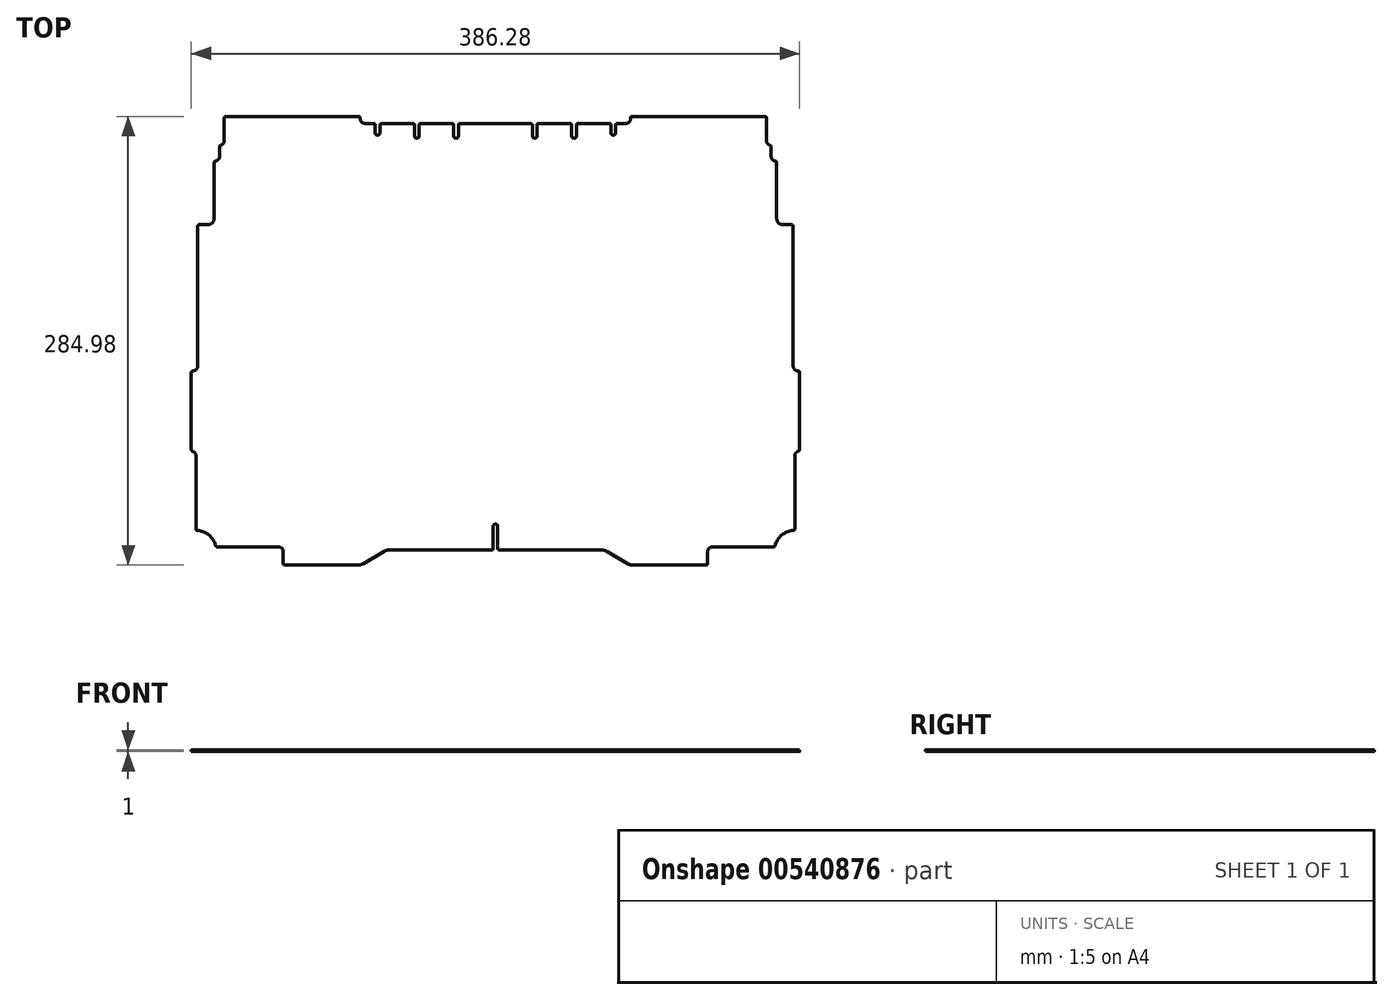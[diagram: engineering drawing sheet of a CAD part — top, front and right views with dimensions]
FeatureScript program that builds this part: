
annotation { "Feature Type Name" : "Feature", "Feature Type Description" : "" }
export const myFeature = defineFeature(function(context is Context, id is Id, definition is map)
    precondition{}
    {
        {
            var Q0;
            Q0=qCreatedBy(makeId("Top.planeOp"),FACE);
            var sketch = newSketch(context, id + "F0", { "sketchPlane" : qUnion([Q0])});
            skLineSegment(sketch, "E0", {"start": v(-80.67, -133.5) * mm, "end": v(-41, -133.5) * mm});
            skLineSegment(sketch, "E1", {"start": v(-38, -136.5) * mm, "end": v(-38, -144.99) * mm});
            skLineSegment(sketch, "E2", {"start": v(-38, -144.99) * mm, "end": v(11.4, -144.99) * mm});
            skLineSegment(sketch, "E3", {"start": v(11.4, -144.99) * mm, "end": v(25.96, -136.34) * mm});
            skLineSegment(sketch, "E4", {"start": v(29.02, -135.5) * mm, "end": v(95.25, -135.5) * mm});
            skLineSegment(sketch, "E5", {"start": v(-93.4, -123.03) * mm, "end": v(-93.4, -75.62) * mm});
            skLineSegment(sketch, "E6", {"start": v(-96.4, -72.62) * mm, "end": v(-96.4, -21.71) * mm});
            skLineSegment(sketch, "E7", {"start": v(-96.4, -21.71) * mm, "end": v(-95.4, -21.71) * mm});
            skLineSegment(sketch, "E8", {"start": v(-92.4, -18.72) * mm, "end": v(-92.4, 71.11) * mm});
            skLineSegment(sketch, "E9", {"start": v(-92.4, 71.11) * mm, "end": v(-85.91, 71.11) * mm});
            skLineSegment(sketch, "E10", {"start": v(-81.92, 75.1) * mm, "end": v(-81.92, 111.54) * mm});
            skLineSegment(sketch, "E11", {"start": v(-81.92, 111.54) * mm, "end": v(-81.42, 111.54) * mm});
            skLineSegment(sketch, "E12", {"start": v(-78.43, 114.53) * mm, "end": v(-78.43, 121.52) * mm});
            skLineSegment(sketch, "E13", {"start": v(-75.43, 124.52) * mm, "end": v(-75.43, 139.99) * mm});
            skLineSegment(sketch, "E14", {"start": v(-75.43, 139.99) * mm, "end": v(10.9, 139.99) * mm});
            skLineSegment(sketch, "E15", {"start": v(10.9, 139.99) * mm, "end": v(10.9, 138.49) * mm});
            skLineSegment(sketch, "E16", {"start": v(13.9, 135.5) * mm, "end": v(20.4, 135.5) * mm});
            skLineSegment(sketch, "E17", {"start": v(96.75, 135.5) * mm, "end": v(96.75, -119.03) * mm});
            skArc(sketch, "E18", {"start": v(96.75, -119.03) * mm, "mid": v(95.7, -119.47) * mm, "end": v(95.25, -120.53) * mm});
            skLineSegment(sketch, "E19", {"start": v(95.25, -120.53) * mm, "end": v(95.25, -135.5) * mm});
            skArc(sketch, "E20", {"start": v(70.3, 127.51) * mm, "mid": v(71.8, 126.01) * mm, "end": v(73.3, 127.51) * mm});
            skLineSegment(sketch, "E21", {"start": v(73.3, 127.51) * mm, "end": v(73.3, 135.5) * mm});
            skLineSegment(sketch, "E22", {"start": v(70.3, 127.51) * mm, "end": v(70.3, 135.5) * mm});
            skLineSegment(sketch, "E23", {"start": v(73.3, 135.5) * mm, "end": v(96.75, 135.5) * mm});
            skLineSegment(sketch, "E24", {"start": v(48.34, 127.51) * mm, "end": v(48.34, 135.5) * mm});
            skLineSegment(sketch, "E25", {"start": v(45.34, 127.51) * mm, "end": v(45.34, 135.5) * mm});
            skArc(sketch, "E26", {"start": v(45.34, 127.51) * mm, "mid": v(46.84, 126.01) * mm, "end": v(48.34, 127.51) * mm});
            skLineSegment(sketch, "E27", {"start": v(23.39, 129.5) * mm, "end": v(23.39, 135.5) * mm});
            skLineSegment(sketch, "E28", {"start": v(20.4, 129.5) * mm, "end": v(20.4, 135.5) * mm});
            skLineSegment(sketch, "E29", {"start": v(48.34, 135.5) * mm, "end": v(70.3, 135.5) * mm});
            skLineSegment(sketch, "E30", {"start": v(23.39, 135.5) * mm, "end": v(45.34, 135.5) * mm});
            skArc(sketch, "E31", {"start": v(-85.91, 71.11) * mm, "mid": v(-83.09, 72.28) * mm, "end": v(-81.92, 75.1) * mm});
            skArc(sketch, "E32", {"start": v(10.9, 138.49) * mm, "mid": v(11.79, 136.37) * mm, "end": v(13.9, 135.5) * mm});
            skArc(sketch, "E33", {"start": v(-95.4, -21.71) * mm, "mid": v(-93.28, -20.84) * mm, "end": v(-92.4, -18.72) * mm});
            skArc(sketch, "E34", {"start": v(-93.4, -75.62) * mm, "mid": v(-94.28, -73.5) * mm, "end": v(-96.4, -72.62) * mm});
            skArc(sketch, "E35", {"start": v(-38, -136.5) * mm, "mid": v(-38.88, -134.39) * mm, "end": v(-41, -133.5) * mm});
            skArc(sketch, "E36", {"start": v(-81.42, 111.54) * mm, "mid": v(-79.3, 112.42) * mm, "end": v(-78.43, 114.53) * mm});
            skArc(sketch, "E37", {"start": v(-78.43, 121.52) * mm, "mid": v(-76.3, 122.4) * mm, "end": v(-75.43, 124.52) * mm});
            skArc(sketch, "E38", {"start": v(29.02, -135.5) * mm, "mid": v(27.44, -135.72) * mm, "end": v(25.96, -136.34) * mm});
            skArc(sketch, "E39", {"start": v(-80.67, -133.5) * mm, "mid": v(-85.15, -125.98) * mm, "end": v(-93.4, -123.03) * mm});
            skArc(sketch, "E40", {"start": v(20.4, 129.5) * mm, "mid": v(21.89, 128) * mm, "end": v(23.39, 129.5) * mm});
            skArc(sketch, "E41.MirrorCS", {"start": v(96.75, -119.03) * mm, "mid": v(97.8, -119.47) * mm, "end": v(98.25, -120.53) * mm});
            skLineSegment(sketch, "E42.MirrorCS", {"start": v(289.9, -21.71) * mm, "end": v(288.9, -21.71) * mm});
            skArc(sketch, "E43.MirrorCS", {"start": v(274.92, 111.54) * mm, "mid": v(272.8, 112.42) * mm, "end": v(271.93, 114.53) * mm});
            skLineSegment(sketch, "E44.MirrorCS", {"start": v(275.42, 111.54) * mm, "end": v(274.92, 111.54) * mm});
            skArc(sketch, "E45.MirrorCS", {"start": v(288.9, -21.71) * mm, "mid": v(286.78, -20.84) * mm, "end": v(285.9, -18.72) * mm});
            skArc(sketch, "E46.MirrorCS", {"start": v(123.2, 127.51) * mm, "mid": v(121.7, 126.01) * mm, "end": v(120.2, 127.51) * mm});
            skArc(sketch, "E47.MirrorCS", {"start": v(148.16, 127.51) * mm, "mid": v(146.66, 126.01) * mm, "end": v(145.16, 127.51) * mm});
            skLineSegment(sketch, "E48.MirrorCS", {"start": v(231.5, -136.5) * mm, "end": v(231.5, -144.99) * mm});
            skLineSegment(sketch, "E49.MirrorCS", {"start": v(173.1, 129.5) * mm, "end": v(173.1, 135.5) * mm});
            skLineSegment(sketch, "E50.MirrorCS", {"start": v(148.16, 127.51) * mm, "end": v(148.16, 135.5) * mm});
            skLineSegment(sketch, "E51.MirrorCS", {"start": v(123.2, 127.51) * mm, "end": v(123.2, 135.5) * mm});
            skLineSegment(sketch, "E52.MirrorCS", {"start": v(271.93, 114.53) * mm, "end": v(271.93, 121.52) * mm});
            skArc(sketch, "E53.MirrorCS", {"start": v(164.48, -135.5) * mm, "mid": v(166.06, -135.72) * mm, "end": v(167.54, -136.34) * mm});
            skLineSegment(sketch, "E54.MirrorCS", {"start": v(179.6, 135.5) * mm, "end": v(173.1, 135.5) * mm});
            skArc(sketch, "E55.MirrorCS", {"start": v(279.41, 71.11) * mm, "mid": v(276.59, 72.28) * mm, "end": v(275.42, 75.1) * mm});
            skLineSegment(sketch, "E56.MirrorCS", {"start": v(145.16, 127.51) * mm, "end": v(145.16, 135.5) * mm});
            skArc(sketch, "E57.MirrorCS", {"start": v(231.5, -136.5) * mm, "mid": v(232.38, -134.39) * mm, "end": v(234.5, -133.5) * mm});
            skLineSegment(sketch, "E58.MirrorCS", {"start": v(285.9, 71.11) * mm, "end": v(279.41, 71.11) * mm});
            skArc(sketch, "E59.MirrorCS", {"start": v(182.6, 138.49) * mm, "mid": v(181.71, 136.37) * mm, "end": v(179.6, 135.5) * mm});
            skLineSegment(sketch, "E60.MirrorCS", {"start": v(182.6, 139.99) * mm, "end": v(182.6, 138.49) * mm});
            skArc(sketch, "E61.MirrorCS", {"start": v(271.93, 121.52) * mm, "mid": v(269.8, 122.4) * mm, "end": v(268.93, 124.52) * mm});
            skArc(sketch, "E62.MirrorCS", {"start": v(173.1, 129.5) * mm, "mid": v(171.61, 128) * mm, "end": v(170.11, 129.5) * mm});
            skArc(sketch, "E63.MirrorCS", {"start": v(286.9, -75.62) * mm, "mid": v(287.78, -73.5) * mm, "end": v(289.9, -72.62) * mm});
            skLineSegment(sketch, "E64.MirrorCS", {"start": v(120.2, 127.51) * mm, "end": v(120.2, 135.5) * mm});
            skLineSegment(sketch, "E65.MirrorCS", {"start": v(170.11, 129.5) * mm, "end": v(170.11, 135.5) * mm});
            skLineSegment(sketch, "E66.MirrorCS", {"start": v(268.93, 124.52) * mm, "end": v(268.93, 139.99) * mm});
            skLineSegment(sketch, "E67.MirrorCS", {"start": v(98.25, -120.53) * mm, "end": v(98.25, -135.5) * mm});
            skLineSegment(sketch, "E68.MirrorCS", {"start": v(231.5, -144.99) * mm, "end": v(182.1, -144.99) * mm});
            skLineSegment(sketch, "E69.MirrorCS", {"start": v(145.16, 135.5) * mm, "end": v(123.2, 135.5) * mm});
            skLineSegment(sketch, "E70.MirrorCS", {"start": v(268.93, 139.99) * mm, "end": v(182.6, 139.99) * mm});
            skLineSegment(sketch, "E71.MirrorCS", {"start": v(164.48, -135.5) * mm, "end": v(98.25, -135.5) * mm});
            skLineSegment(sketch, "E72.MirrorCS", {"start": v(286.9, -123.03) * mm, "end": v(286.9, -75.62) * mm});
            skLineSegment(sketch, "E73.MirrorCS", {"start": v(170.11, 135.5) * mm, "end": v(148.16, 135.5) * mm});
            skLineSegment(sketch, "E74.MirrorCS", {"start": v(274.17, -133.5) * mm, "end": v(234.5, -133.5) * mm});
            skArc(sketch, "E75.MirrorCS", {"start": v(274.17, -133.5) * mm, "mid": v(278.65, -125.98) * mm, "end": v(286.9, -123.03) * mm});
            skLineSegment(sketch, "E76.MirrorCS", {"start": v(275.42, 75.1) * mm, "end": v(275.42, 111.54) * mm});
            skLineSegment(sketch, "E77.MirrorCS", {"start": v(182.1, -144.99) * mm, "end": v(167.54, -136.34) * mm});
            skLineSegment(sketch, "E78.MirrorCS", {"start": v(289.9, -72.62) * mm, "end": v(289.9, -21.71) * mm});
            skLineSegment(sketch, "E79.MirrorCS", {"start": v(285.9, -18.72) * mm, "end": v(285.9, 71.11) * mm});
            skLineSegment(sketch, "E80.MirrorCS", {"start": v(120.2, 135.5) * mm, "end": v(96.75, 135.5) * mm});
            skSolve(sketch);
        }
        {
            var Q0;
            Q0=makeQuery(id+"F0.imprint","IMPRINT",FACE,{"disambiguationData":[TD([[makeQuery(id+"F0.imprint","IMPRINT",EDGE,{"derivedFrom":sQuery(id+"F0.wireOp",EDGE,"E0")}),1.0]])]});
            var Q1;
            Q1=makeQuery(id+"F0.imprint","IMPRINT",FACE,{"disambiguationData":[TD([[makeQuery(id+"F0.imprint","IMPRINT",EDGE,{"derivedFrom":sQuery(id+"F0.wireOp",EDGE,"E17")}),1.0]])]});
            extrude(context, id + "F1", {"entities" : qUnion([Q0, Q1]), "depth" : 1 * mm, "offsetDistance" : 25 * mm});
        }
        {
            var Q0;
            Q0=makeQuery(id+"F1.opExtrude","SWEPT_EDGE",EDGE,{"disambiguationData":[OSD([sQuery(id+"F0.wireOp",EDGE,"E1"),sQuery(id+"F0.wireOp",EDGE,"E2")])]});
            var Q1;
            Q1=makeQuery(id+"F1.opExtrude","SWEPT_EDGE",EDGE,{"disambiguationData":[OSD([sQuery(id+"F0.wireOp",EDGE,"E0"),sQuery(id+"F0.wireOp",EDGE,"E39")])]});
            var Q2;
            Q2=makeQuery(id+"F1.opExtrude","SWEPT_EDGE",EDGE,{"disambiguationData":[OSD([sQuery(id+"F0.wireOp",EDGE,"E5"),sQuery(id+"F0.wireOp",EDGE,"E39")])]});
            var Q3;
            Q3=makeQuery(id+"F1.opExtrude","SWEPT_EDGE",EDGE,{"disambiguationData":[OSD([sQuery(id+"F0.wireOp",EDGE,"E6"),sQuery(id+"F0.wireOp",EDGE,"E34")])]});
            var Q4;
            Q4=makeQuery(id+"F1.opExtrude","SWEPT_EDGE",EDGE,{"disambiguationData":[OSD([sQuery(id+"F0.wireOp",EDGE,"E6"),sQuery(id+"F0.wireOp",EDGE,"E7")])]});
            var Q5;
            Q5=makeQuery(id+"F1.opExtrude","SWEPT_EDGE",EDGE,{"disambiguationData":[OSD([sQuery(id+"F0.wireOp",EDGE,"E8"),sQuery(id+"F0.wireOp",EDGE,"E9")])]});
            var Q6;
            Q6=makeQuery(id+"F1.opExtrude","SWEPT_EDGE",EDGE,{"disambiguationData":[OSD([sQuery(id+"F0.wireOp",EDGE,"E10"),sQuery(id+"F0.wireOp",EDGE,"E11")])]});
            var Q7;
            Q7=makeQuery(id+"F1.opExtrude","SWEPT_EDGE",EDGE,{"disambiguationData":[OSD([sQuery(id+"F0.wireOp",EDGE,"E12"),sQuery(id+"F0.wireOp",EDGE,"E37")])]});
            var Q8;
            Q8=makeQuery(id+"F1.opExtrude","SWEPT_EDGE",EDGE,{"disambiguationData":[OSD([sQuery(id+"F0.wireOp",EDGE,"E13"),sQuery(id+"F0.wireOp",EDGE,"E14")])]});
            var Q9;
            Q9=makeQuery(id+"F1.opExtrude","SWEPT_EDGE",EDGE,{"disambiguationData":[OSD([sQuery(id+"F0.wireOp",EDGE,"E14"),sQuery(id+"F0.wireOp",EDGE,"E15")])]});
            var Q10;
            Q10=makeQuery(id+"F1.opExtrude","SWEPT_EDGE",EDGE,{"disambiguationData":[OSD([sQuery(id+"F0.wireOp",EDGE,"E16"),sQuery(id+"F0.wireOp",EDGE,"E28")])]});
            var Q11;
            Q11=makeQuery(id+"F1.opExtrude","SWEPT_EDGE",EDGE,{"disambiguationData":[OSD([sQuery(id+"F0.wireOp",EDGE,"E27"),sQuery(id+"F0.wireOp",EDGE,"E30")])]});
            var Q12;
            Q12=makeQuery(id+"F1.opExtrude","SWEPT_EDGE",EDGE,{"disambiguationData":[OSD([sQuery(id+"F0.wireOp",EDGE,"E25"),sQuery(id+"F0.wireOp",EDGE,"E30")])]});
            var Q13;
            Q13=makeQuery(id+"F1.opExtrude","SWEPT_EDGE",EDGE,{"disambiguationData":[OSD([sQuery(id+"F0.wireOp",EDGE,"E24"),sQuery(id+"F0.wireOp",EDGE,"E29")])]});
            var Q14;
            Q14=makeQuery(id+"F1.opExtrude","SWEPT_EDGE",EDGE,{"disambiguationData":[OSD([sQuery(id+"F0.wireOp",EDGE,"E22"),sQuery(id+"F0.wireOp",EDGE,"E29")])]});
            var Q15;
            Q15=makeQuery(id+"F1.opExtrude","SWEPT_EDGE",EDGE,{"disambiguationData":[OSD([sQuery(id+"F0.wireOp",EDGE,"E21"),sQuery(id+"F0.wireOp",EDGE,"E23")])]});
            var Q16;
            Q16=makeQuery(id+"F1.opExtrude","SWEPT_EDGE",EDGE,{"disambiguationData":[OSD([sQuery(id+"F0.wireOp",EDGE,"E64.MirrorCS"),sQuery(id+"F0.wireOp",EDGE,"E80.MirrorCS")])]});
            var Q17;
            Q17=makeQuery(id+"F1.opExtrude","SWEPT_EDGE",EDGE,{"disambiguationData":[OSD([sQuery(id+"F0.wireOp",EDGE,"E51.MirrorCS"),sQuery(id+"F0.wireOp",EDGE,"E69.MirrorCS")])]});
            var Q18;
            Q18=makeQuery(id+"F1.opExtrude","SWEPT_EDGE",EDGE,{"disambiguationData":[OSD([sQuery(id+"F0.wireOp",EDGE,"E56.MirrorCS"),sQuery(id+"F0.wireOp",EDGE,"E69.MirrorCS")])]});
            var Q19;
            Q19=makeQuery(id+"F1.opExtrude","SWEPT_EDGE",EDGE,{"disambiguationData":[OSD([sQuery(id+"F0.wireOp",EDGE,"E50.MirrorCS"),sQuery(id+"F0.wireOp",EDGE,"E73.MirrorCS")])]});
            var Q20;
            Q20=makeQuery(id+"F1.opExtrude","SWEPT_EDGE",EDGE,{"disambiguationData":[OSD([sQuery(id+"F0.wireOp",EDGE,"E65.MirrorCS"),sQuery(id+"F0.wireOp",EDGE,"E73.MirrorCS")])]});
            var Q21;
            Q21=makeQuery(id+"F1.opExtrude","SWEPT_EDGE",EDGE,{"disambiguationData":[OSD([sQuery(id+"F0.wireOp",EDGE,"E49.MirrorCS"),sQuery(id+"F0.wireOp",EDGE,"E54.MirrorCS")])]});
            var Q22;
            Q22=makeQuery(id+"F1.opExtrude","SWEPT_EDGE",EDGE,{"disambiguationData":[OSD([sQuery(id+"F0.wireOp",EDGE,"E60.MirrorCS"),sQuery(id+"F0.wireOp",EDGE,"E70.MirrorCS")])]});
            var Q23;
            Q23=makeQuery(id+"F1.opExtrude","SWEPT_EDGE",EDGE,{"disambiguationData":[OSD([sQuery(id+"F0.wireOp",EDGE,"E66.MirrorCS"),sQuery(id+"F0.wireOp",EDGE,"E70.MirrorCS")])]});
            var Q24;
            Q24=makeQuery(id+"F1.opExtrude","SWEPT_EDGE",EDGE,{"disambiguationData":[OSD([sQuery(id+"F0.wireOp",EDGE,"E52.MirrorCS"),sQuery(id+"F0.wireOp",EDGE,"E61.MirrorCS")])]});
            var Q25;
            Q25=makeQuery(id+"F1.opExtrude","SWEPT_EDGE",EDGE,{"disambiguationData":[OSD([sQuery(id+"F0.wireOp",EDGE,"E44.MirrorCS"),sQuery(id+"F0.wireOp",EDGE,"E76.MirrorCS")])]});
            var Q26;
            Q26=makeQuery(id+"F1.opExtrude","SWEPT_EDGE",EDGE,{"disambiguationData":[OSD([sQuery(id+"F0.wireOp",EDGE,"E58.MirrorCS"),sQuery(id+"F0.wireOp",EDGE,"E79.MirrorCS")])]});
            var Q27;
            Q27=makeQuery(id+"F1.opExtrude","SWEPT_EDGE",EDGE,{"disambiguationData":[OSD([sQuery(id+"F0.wireOp",EDGE,"E42.MirrorCS"),sQuery(id+"F0.wireOp",EDGE,"E78.MirrorCS")])]});
            var Q28;
            Q28=makeQuery(id+"F1.opExtrude","SWEPT_EDGE",EDGE,{"disambiguationData":[OSD([sQuery(id+"F0.wireOp",EDGE,"E63.MirrorCS"),sQuery(id+"F0.wireOp",EDGE,"E78.MirrorCS")])]});
            var Q29;
            Q29=makeQuery(id+"F1.opExtrude","SWEPT_EDGE",EDGE,{"disambiguationData":[OSD([sQuery(id+"F0.wireOp",EDGE,"E72.MirrorCS"),sQuery(id+"F0.wireOp",EDGE,"E75.MirrorCS")])]});
            var Q30;
            Q30=makeQuery(id+"F1.opExtrude","SWEPT_EDGE",EDGE,{"disambiguationData":[OSD([sQuery(id+"F0.wireOp",EDGE,"E74.MirrorCS"),sQuery(id+"F0.wireOp",EDGE,"E75.MirrorCS")])]});
            var Q31;
            Q31=makeQuery(id+"F1.opExtrude","SWEPT_EDGE",EDGE,{"disambiguationData":[OSD([sQuery(id+"F0.wireOp",EDGE,"E48.MirrorCS"),sQuery(id+"F0.wireOp",EDGE,"E68.MirrorCS")])]});
            var Q32;
            Q32=makeQuery(id+"F1.opExtrude","SWEPT_EDGE",EDGE,{"disambiguationData":[OSD([sQuery(id+"F0.wireOp",EDGE,"E67.MirrorCS"),sQuery(id+"F0.wireOp",EDGE,"E71.MirrorCS")])]});
            var Q33;
            Q33=makeQuery(id+"F1.opExtrude","SWEPT_EDGE",EDGE,{"disambiguationData":[OSD([sQuery(id+"F0.wireOp",EDGE,"E4"),sQuery(id+"F0.wireOp",EDGE,"E19")])]});
            fillet(context, id + "F2", {"entities" : qUnion([Q0, Q1, Q2, Q3, Q4, Q5, Q6, Q7, Q8, Q9, Q10, Q11, Q12, Q13, Q14, Q15, Q16, Q17, Q18, Q19, Q20, Q21, Q22, Q23, Q24, Q25, Q26, Q27, Q28, Q29, Q30, Q31, Q32, Q33]), "radius" : 1 * mm, "tangentPropagation" : true, "allowEdgeOverflow" : false});
        }
        {
            var Q0;
            Q0=makeQuery(id+"F1.opExtrude","SWEPT_EDGE",EDGE,{"disambiguationData":[OSD([sQuery(id+"F0.wireOp",EDGE,"E68.MirrorCS"),sQuery(id+"F0.wireOp",EDGE,"E77.MirrorCS")])]});
            var Q1;
            Q1=makeQuery(id+"F1.opExtrude","SWEPT_EDGE",EDGE,{"disambiguationData":[OSD([sQuery(id+"F0.wireOp",EDGE,"E2"),sQuery(id+"F0.wireOp",EDGE,"E3")])]});
            fillet(context, id + "F3", {"entities" : qUnion([Q0, Q1]), "radius" : 5 * mm, "tangentPropagation" : true, "allowEdgeOverflow" : false});
        }
    });
